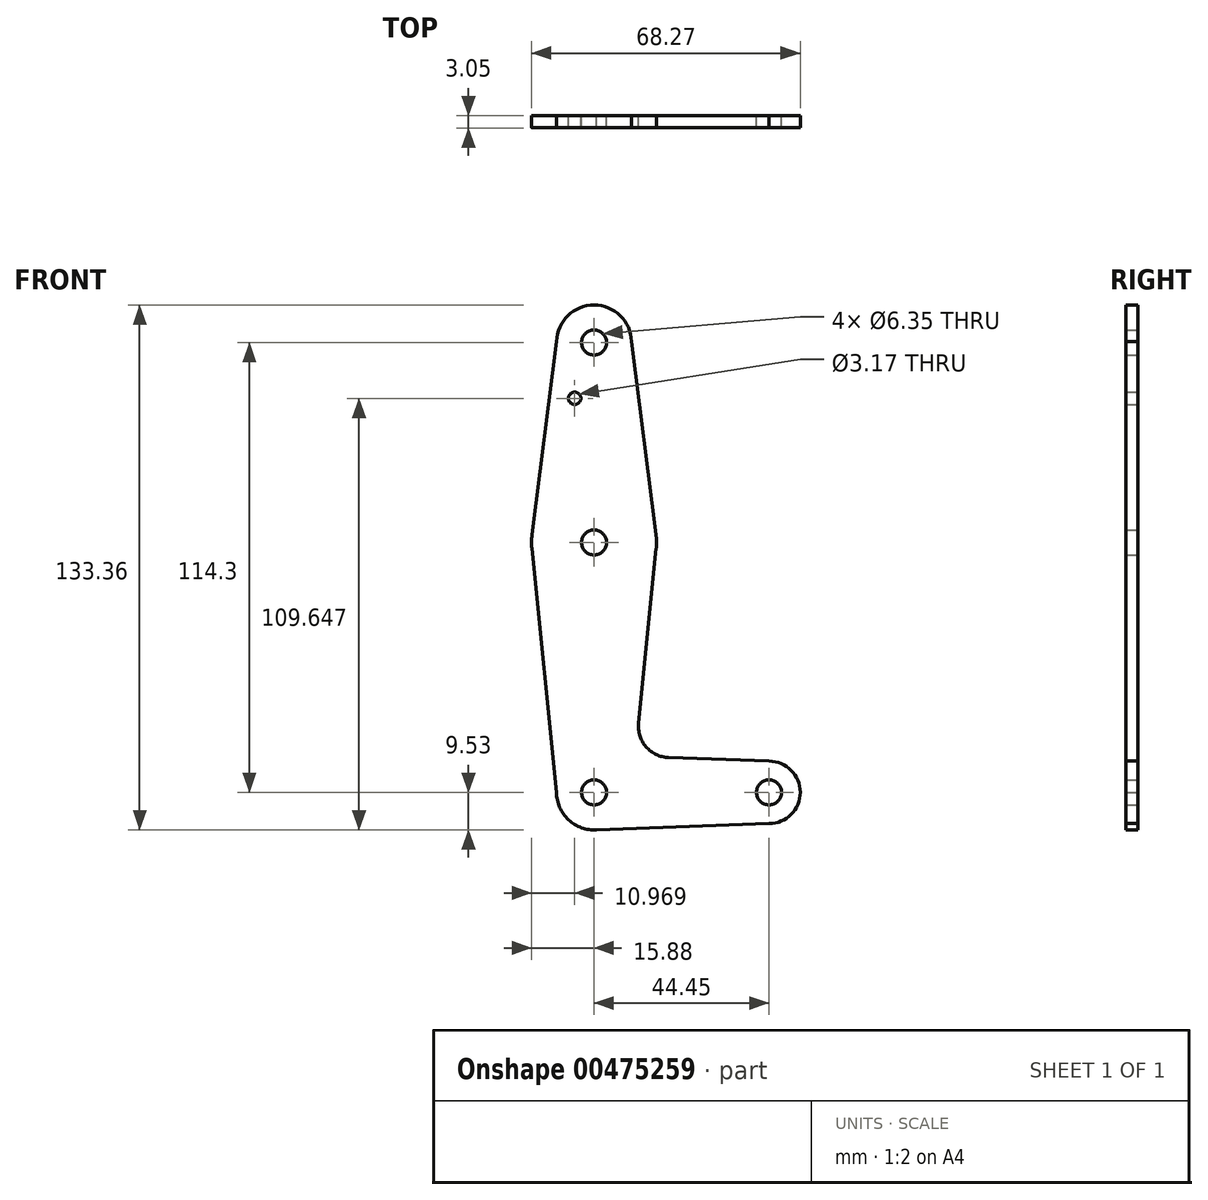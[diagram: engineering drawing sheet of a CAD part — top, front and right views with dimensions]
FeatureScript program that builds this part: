
annotation { "Feature Type Name" : "Feature", "Feature Type Description" : "" }
export const myFeature = defineFeature(function(context is Context, id is Id, definition is map)
    precondition{}
    {
        {
            var Q0;
            Q0=qCreatedBy(makeId("Front.planeOp"),FACE);
            var sketch = newSketch(context, id + "F0", { "sketchPlane" : qUnion([Q0])});
            skLineSegment(sketch, "E0", {"start": v(0, 114.3) * mm, "end": v(0, 0) * mm, "construction": true});
            skCircle(sketch, "E1", {"center": v(0, 114.3) * mm, "radius": 9.53 * mm});
            skCircle(sketch, "E2", {"center": v(0, 0) * mm, "radius": 9.53 * mm});
            skCircle(sketch, "E3", {"center": v(0, 63.5) * mm, "radius": 15.88 * mm});
            skLineSegment(sketch, "E4", {"start": v(0, 0) * mm, "end": v(44.45, 0) * mm, "construction": true});
            skCircle(sketch, "E5", {"center": v(44.45, 0) * mm, "radius": 7.94 * mm});
            skLineSegment(sketch, "E6", {"start": v(-9.52, 114.55) * mm, "end": v(-15.75, 65.5) * mm});
            skLineSegment(sketch, "E7", {"start": v(9.52, 114.55) * mm, "end": v(15.75, 65.5) * mm});
            skLineSegment(sketch, "E8", {"start": v(0, -9.52) * mm, "end": v(44.45, -7.94) * mm});
            skCircle(sketch, "E9", {"center": v(0, 114.3) * mm, "radius": 3.18 * mm});
            skCircle(sketch, "E10", {"center": v(-4.91, 100.12) * mm, "radius": 1.59 * mm});
            skCircle(sketch, "E11", {"center": v(0, 63.5) * mm, "radius": 3.18 * mm});
            skCircle(sketch, "E12", {"center": v(0, 0) * mm, "radius": 3.18 * mm});
            skCircle(sketch, "E13", {"center": v(44.45, 0) * mm, "radius": 3.18 * mm});
            skLineSegment(sketch, "E14", {"start": v(-9.53, 0) * mm, "end": v(-15.8, 61.9) * mm});
            skLineSegment(sketch, "E15", {"start": v(11.3, 17.6) * mm, "end": v(15.8, 61.9) * mm});
            skLineSegment(sketch, "E16", {"start": v(18.93, 8.85) * mm, "end": v(44.45, 7.94) * mm});
            skArc(sketch, "E17.filletArc", {"start": v(11.3, 17.6) * mm, "mid": v(13.22, 11.57) * mm, "end": v(18.93, 8.85) * mm});
            skSolve(sketch);
        }
        {
            var Q0;
            Q0 = qSketchRegion(id + "F0", true);
            extrude(context, id + "F1", {"entities" : qUnion([Q0]), "depth" : 3.05 * mm});
        }
    });
